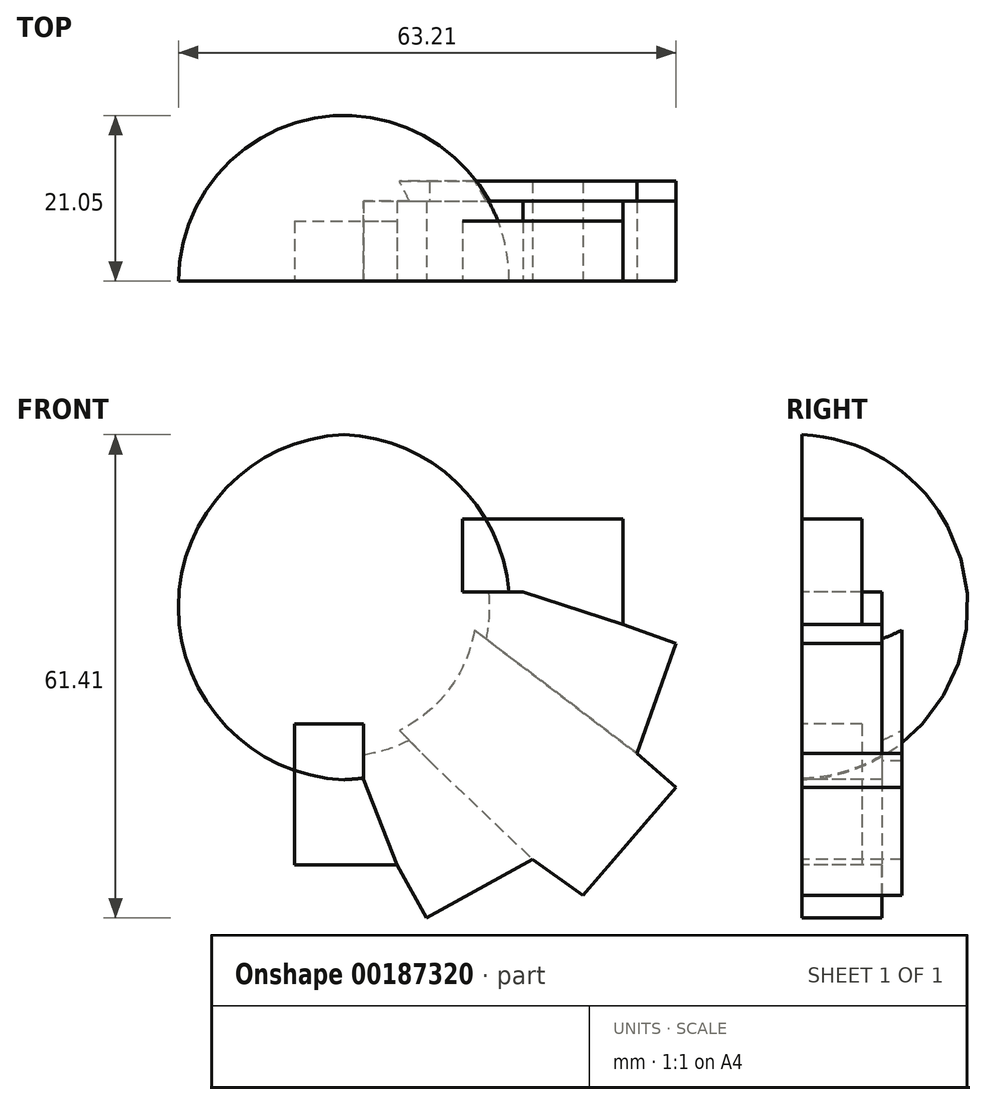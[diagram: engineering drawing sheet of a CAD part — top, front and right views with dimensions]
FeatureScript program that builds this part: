
annotation { "Feature Type Name" : "Feature", "Feature Type Description" : "" }
export const myFeature = defineFeature(function(context is Context, id is Id, definition is map)
    precondition{}
    {
        {
            var Q0;
            Q0=qCreatedBy(makeId("Front.planeOp"),FACE);
            var sketch = newSketch(context, id + "F0", { "sketchPlane" : qUnion([Q0])});
            skLineSegment(sketch, "E0", {"start": v(-11.54, -19.3) * mm, "end": v(-11.54, -30.56) * mm});
            skLineSegment(sketch, "E1", {"start": v(-11.54, -30.56) * mm, "end": v(1.51, -30.56) * mm});
            skLineSegment(sketch, "E2", {"start": v(1.51, -30.56) * mm, "end": v(5.22, -37.3) * mm});
            skLineSegment(sketch, "E3", {"start": v(5.22, -37.3) * mm, "end": v(18.74, -29.84) * mm});
            skLineSegment(sketch, "E4", {"start": v(18.74, -29.84) * mm, "end": v(25.14, -34.4) * mm});
            skLineSegment(sketch, "E5", {"start": v(25.14, -34.4) * mm, "end": v(36.95, -20.67) * mm});
            skLineSegment(sketch, "E6", {"start": v(36.95, -20.67) * mm, "end": v(31.97, -16.39) * mm});
            skLineSegment(sketch, "E7", {"start": v(31.97, -16.39) * mm, "end": v(36.95, -2.4) * mm});
            skLineSegment(sketch, "E8", {"start": v(36.95, -2.4) * mm, "end": v(30.2, 0) * mm});
            skLineSegment(sketch, "E9", {"start": v(30.2, 0) * mm, "end": v(30.2, 13.4) * mm});
            skLineSegment(sketch, "E10", {"start": v(30.2, 13.4) * mm, "end": v(16.2, 13.4) * mm});
            skCircle(sketch, "E11", {"center": v(-4.33, 2.2) * mm, "radius": 21.94 * mm});
            skPoint(sketch, "E11.first.point", {"position": v(-5.21, 24.12) * mm});
            skPoint(sketch, "E11.second.point", {"position": v(-26.15, 0) * mm});
            skPoint(sketch, "E11.third.point", {"position": v(8.47, -15.62) * mm});
            skLineSegment(sketch, "E12", {"start": v(17.53, 4.12) * mm, "end": v(30.2, 0) * mm});
            skLineSegment(sketch, "E13", {"start": v(16.52, -4.64) * mm, "end": v(31.97, -16.39) * mm});
            skLineSegment(sketch, "E14", {"start": v(5.64, -17.34) * mm, "end": v(18.74, -29.84) * mm});
            skLineSegment(sketch, "E15", {"start": v(-2.77, -19.68) * mm, "end": v(1.51, -30.56) * mm});
            skLineSegment(sketch, "E16", {"start": v(16.2, 13.4) * mm, "end": v(14.54, 13.4) * mm});
            skLineSegment(sketch, "E17", {"start": v(-11.54, -19.3) * mm, "end": v(-11.54, -18.51) * mm});
            skLineSegment(sketch, "E18", {"start": v(-5.21, 24.12) * mm, "end": v(-5.21, -19.72) * mm});
            skLineSegment(sketch, "E19", {"start": v(16.52, -4.64) * mm, "end": v(11.3, -0.67) * mm});
            skLineSegment(sketch, "E20", {"start": v(11.3, -0.67) * mm, "end": v(1.01, -12.63) * mm});
            skLineSegment(sketch, "E21", {"start": v(1.01, -12.63) * mm, "end": v(5.64, -17.34) * mm});
            skLineSegment(sketch, "E22", {"start": v(14.54, 13.4) * mm, "end": v(9.84, 13.4) * mm});
            skLineSegment(sketch, "E23", {"start": v(9.84, 13.4) * mm, "end": v(9.84, 4.12) * mm});
            skLineSegment(sketch, "E24", {"start": v(9.84, 4.12) * mm, "end": v(17.53, 4.12) * mm});
            skLineSegment(sketch, "E25", {"start": v(9.84, 4.12) * mm, "end": v(11.3, -0.67) * mm});
            skLineSegment(sketch, "E26", {"start": v(-11.54, -18.51) * mm, "end": v(-11.54, -12.63) * mm});
            skLineSegment(sketch, "E27", {"start": v(-11.54, -12.63) * mm, "end": v(-2.77, -12.63) * mm});
            skLineSegment(sketch, "E28", {"start": v(-2.77, -12.63) * mm, "end": v(-2.77, -19.68) * mm});
            skLineSegment(sketch, "E29", {"start": v(-2.77, -12.63) * mm, "end": v(1.01, -12.63) * mm});
            skSolve(sketch);
        }
        {
            var Q0;
            {var subQ2=sQuery(id+"F0.wireOp",EDGE,"E18");Q0=makeQuery(id+"F0.imprint","IMPRINT",FACE,{"disambiguationData":[TD([[makeQuery(id+"F0.imprint","IMPRINT",EDGE,{"derivedFrom":subQ2}),-1.0]])]});}
            var Q1;
            Q1=sQuery(id+"F0.wireOp",EDGE,"E18");
            revolve(context, id + "F1", {"entities" : qUnion([Q0]), "axis" : qUnion([Q1]), "revolveType" : RevolveType.ONE_DIRECTION, "angle" : 180 * degree});
        }
        {
            var Q0;
            Q0=makeQuery(id+"F0.imprint","IMPRINT",FACE,{"disambiguationData":[TD([[makeQuery(id+"F0.imprint","IMPRINT",EDGE,{"derivedFrom":sQuery(id+"F0.wireOp",EDGE,"E4")}),1.0]])]});
            var Q1;
            {var subQ0=sQuery(id+"F0.wireOp",EDGE,"E19");Q1=makeQuery(id+"F0.imprint","IMPRINT",FACE,{"disambiguationData":[TD([[makeQuery(id+"F0.imprint","IMPRINT",EDGE,{"derivedFrom":subQ0}),1.0]])]});}
            extrude(context, id + "F2", {"entities" : qUnion([Q0, Q1]), "oppositeDirection" : true, "depth" : 12.7 * mm});
        }
        {
            var Q0;
            {var subQ2=sQuery(id+"F0.wireOp",EDGE,"E19");Q0=makeQuery(id+"F0.imprint","IMPRINT",FACE,{"disambiguationData":[TD([[makeQuery(id+"F0.imprint","IMPRINT",EDGE,{"derivedFrom":subQ2}),-1.0]])]});}
            var Q1;
            {var subQ0=sQuery(id+"F0.wireOp",EDGE,"E21");Q1=makeQuery(id+"F0.imprint","IMPRINT",FACE,{"disambiguationData":[TD([[makeQuery(id+"F0.imprint","IMPRINT",EDGE,{"derivedFrom":subQ0}),-1.0]])]});}
            var Q2;
            Q2=makeQuery(id+"F0.imprint","IMPRINT",FACE,{"disambiguationData":[TD([[makeQuery(id+"F0.imprint","IMPRINT",EDGE,{"derivedFrom":sQuery(id+"F0.wireOp",EDGE,"E2")}),1.0]])]});
            var Q3;
            Q3=makeQuery(id+"F0.imprint","IMPRINT",FACE,{"disambiguationData":[TD([[makeQuery(id+"F0.imprint","IMPRINT",EDGE,{"derivedFrom":sQuery(id+"F0.wireOp",EDGE,"E7")}),1.0]])]});
            extrude(context, id + "F3", {"entities" : qUnion([Q0, Q1, Q2, Q3]), "operationType" : NewBodyOperationType.ADD, "oppositeDirection" : true, "depth" : 10.16 * mm});
        }
        {
            var Q0;
            {var subQ2=sQuery(id+"F0.wireOp",EDGE,"E22");Q0=makeQuery(id+"F0.imprint","IMPRINT",FACE,{"disambiguationData":[TD([[makeQuery(id+"F0.imprint","IMPRINT",EDGE,{"derivedFrom":subQ2}),1.0]])]});}
            var Q1;
            Q1=makeQuery(id+"F0.imprint","IMPRINT",FACE,{"disambiguationData":[TD([[makeQuery(id+"F0.imprint","IMPRINT",EDGE,{"derivedFrom":sQuery(id+"F0.wireOp",EDGE,"E9")}),1.0]])]});
            var Q2;
            Q2=makeQuery(id+"F0.imprint","IMPRINT",FACE,{"disambiguationData":[TD([[makeQuery(id+"F0.imprint","IMPRINT",EDGE,{"derivedFrom":sQuery(id+"F0.wireOp",EDGE,"E0")}),1.0]])]});
            var Q3;
            {var subQ0=sQuery(id+"F0.wireOp",EDGE,"E26");Q3=makeQuery(id+"F0.imprint","IMPRINT",FACE,{"disambiguationData":[TD([[makeQuery(id+"F0.imprint","IMPRINT",EDGE,{"derivedFrom":subQ0}),-1.0]])]});}
            var Q4;
            {var subQ0=sQuery(id+"F0.wireOp",EDGE,"E28");Q4=makeQuery(id+"F0.imprint","IMPRINT",FACE,{"disambiguationData":[TD([[makeQuery(id+"F0.imprint","IMPRINT",EDGE,{"derivedFrom":subQ0}),-1.0]])]});}
            extrude(context, id + "F4", {"entities" : qUnion([Q0, Q1, Q2, Q3, Q4]), "oppositeDirection" : true, "depth" : 7.62 * mm});
        }
    });
